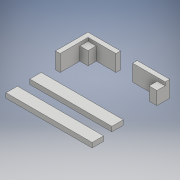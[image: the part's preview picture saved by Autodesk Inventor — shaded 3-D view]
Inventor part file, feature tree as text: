
AUTODESK INVENTOR PART (.ipt)
format: ipt  version: 2018 (Build 220112000, 112)  size: 209,920 bytes
history: native  units: mm
features: extrude x4, sketch x4
ambient origin geometry x8: Origin, YZ Plane, XZ Plane, XY Plane, X Axis, Y Axis, Z Axis, Center Point
bodies: Body1 (feature_tree)
feature tree (8):
  extrude  "Extrusão3"  Depth=10.0mm
  extrude  "Extrusão4"  Depth=5.0mm
  extrude  "Extrusão5"  Depth=5.0mm
  extrude  "Extrusão6"  Depth=2.9mm
  sketch  "Esboço1"  dims[d3=10.0mm d4=20.0mm]
  sketch  "Esboço3"  dims[d6=20.0mm d7=5.0mm]
  sketch  "Esboço4"  dims[d8=5.0mm d9=3.0mm]
  sketch  "Esboço5"  dims[d10=3.0mm d11=20.0mm d14=5.0mm d15=5.0mm d16=3.0mm d17=5.0mm d18=5.0mm d19=3.0mm d20=5.0mm d21=20.0mm d22=10.0mm d23=5.0mm d33=0.1mm d34=0.1mm d35=0.1mm d36=0.1mm d37=0.1mm d38=0.1mm d40=0.1mm d41=0.1mm d43=0.1mm d44=0.1mm d45=0.1mm d46=0.1mm d47=0.1mm d48=0.1mm d49=0.1mm d50=0.1mm d51=0.1mm d52=0.1mm d53=0.1mm d54=0.1mm d55=0.1mm d56=0.1mm d57=10.0mm d58=0.0mm d60=4.8mm d61=5.0mm d62=4.8mm d63=5.0mm d64=2.0mm d65=0.0mm d66=20.0mm d67=0.0mm d68=52.5mm d69=50.0mm d72=7.0mm d73=7.0mm d74=7.5mm d75=2.9mm d76=0.0mm]
